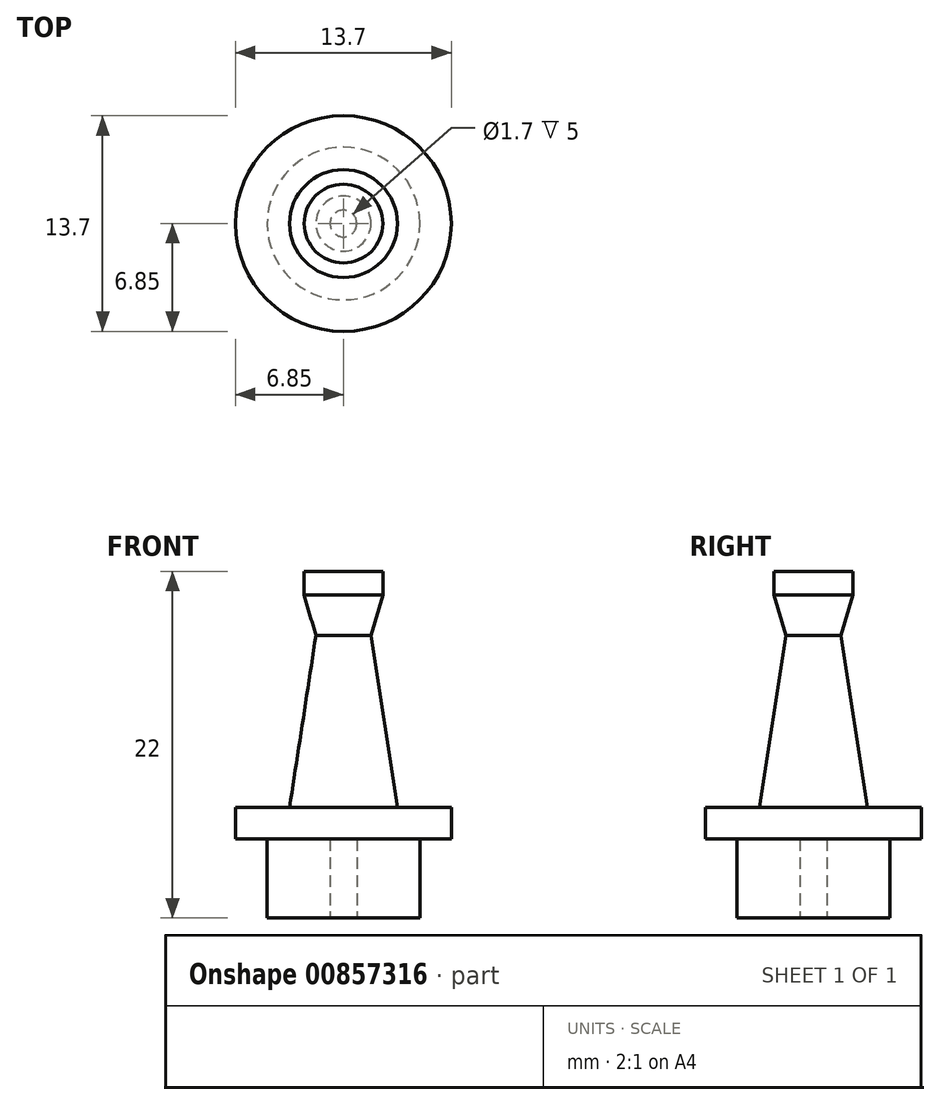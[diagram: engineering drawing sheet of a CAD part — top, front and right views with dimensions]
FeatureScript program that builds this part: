
annotation { "Feature Type Name" : "Feature", "Feature Type Description" : "" }
export const myFeature = defineFeature(function(context is Context, id is Id, definition is map)
    precondition{}
    {
        {
            var Q0;
            Q0=qCreatedBy(makeId("Front.planeOp"),FACE);
            var sketch = newSketch(context, id + "F0", { "sketchPlane" : qUnion([Q0])});
            skLineSegment(sketch, "E0", {"start": v(0, 0) * mm, "end": v(0, 30.67) * mm, "construction": true});
            skLineSegment(sketch, "E1", {"start": v(0, 5) * mm, "end": v(0.85, 5) * mm});
            skLineSegment(sketch, "E2", {"start": v(0.85, 5) * mm, "end": v(0.85, 0) * mm});
            skLineSegment(sketch, "E3", {"start": v(0.85, 0) * mm, "end": v(4.85, 0) * mm});
            skLineSegment(sketch, "E4", {"start": v(4.85, 0) * mm, "end": v(4.85, 5) * mm});
            skLineSegment(sketch, "E5", {"start": v(4.85, 5) * mm, "end": v(6.85, 5) * mm});
            skLineSegment(sketch, "E6", {"start": v(6.85, 5) * mm, "end": v(6.85, 7) * mm});
            skLineSegment(sketch, "E7", {"start": v(6.85, 7) * mm, "end": v(0, 7) * mm});
            skLineSegment(sketch, "E8", {"start": v(0, 7) * mm, "end": v(0, 5) * mm});
            skLineSegment(sketch, "E9", {"start": v(0, 22) * mm, "end": v(2.5, 22) * mm});
            skLineSegment(sketch, "E10", {"start": v(2.5, 22) * mm, "end": v(2.5, 20.5) * mm});
            skLineSegment(sketch, "E11", {"start": v(1.75, 17.94) * mm, "end": v(2.5, 20.5) * mm});
            skLineSegment(sketch, "E12", {"start": v(0, 22) * mm, "end": v(0, 7) * mm});
            skLineSegment(sketch, "E13", {"start": v(1.75, 17.94) * mm, "end": v(3.43, 7) * mm});
            skSolve(sketch);
        }
        {
            var Q0;
            Q0=makeQuery(id+"F0.imprint","IMPRINT",FACE,{"disambiguationData":[TD([[makeQuery(id+"F0.imprint","IMPRINT",EDGE,{"derivedFrom":sQuery(id+"F0.wireOp",EDGE,"E1")}),1.0]])]});
            var Q1;
            Q1=makeQuery(id+"F0.imprint","IMPRINT",FACE,{"disambiguationData":[TD([[makeQuery(id+"F0.imprint","IMPRINT",EDGE,{"derivedFrom":sQuery(id+"F0.wireOp",EDGE,"E9")}),-1.0]])]});
            var Q2;
            Q2=sQuery(id+"F0.wireOp",EDGE,"E0");
            revolve(context, id + "F1", {"surfaceOperationType" : NewSurfaceOperationType.NEW, "entities" : qUnion([Q0, Q1]), "axis" : qUnion([Q2]), "revolveType" : RevolveType.FULL});
        }
    });
